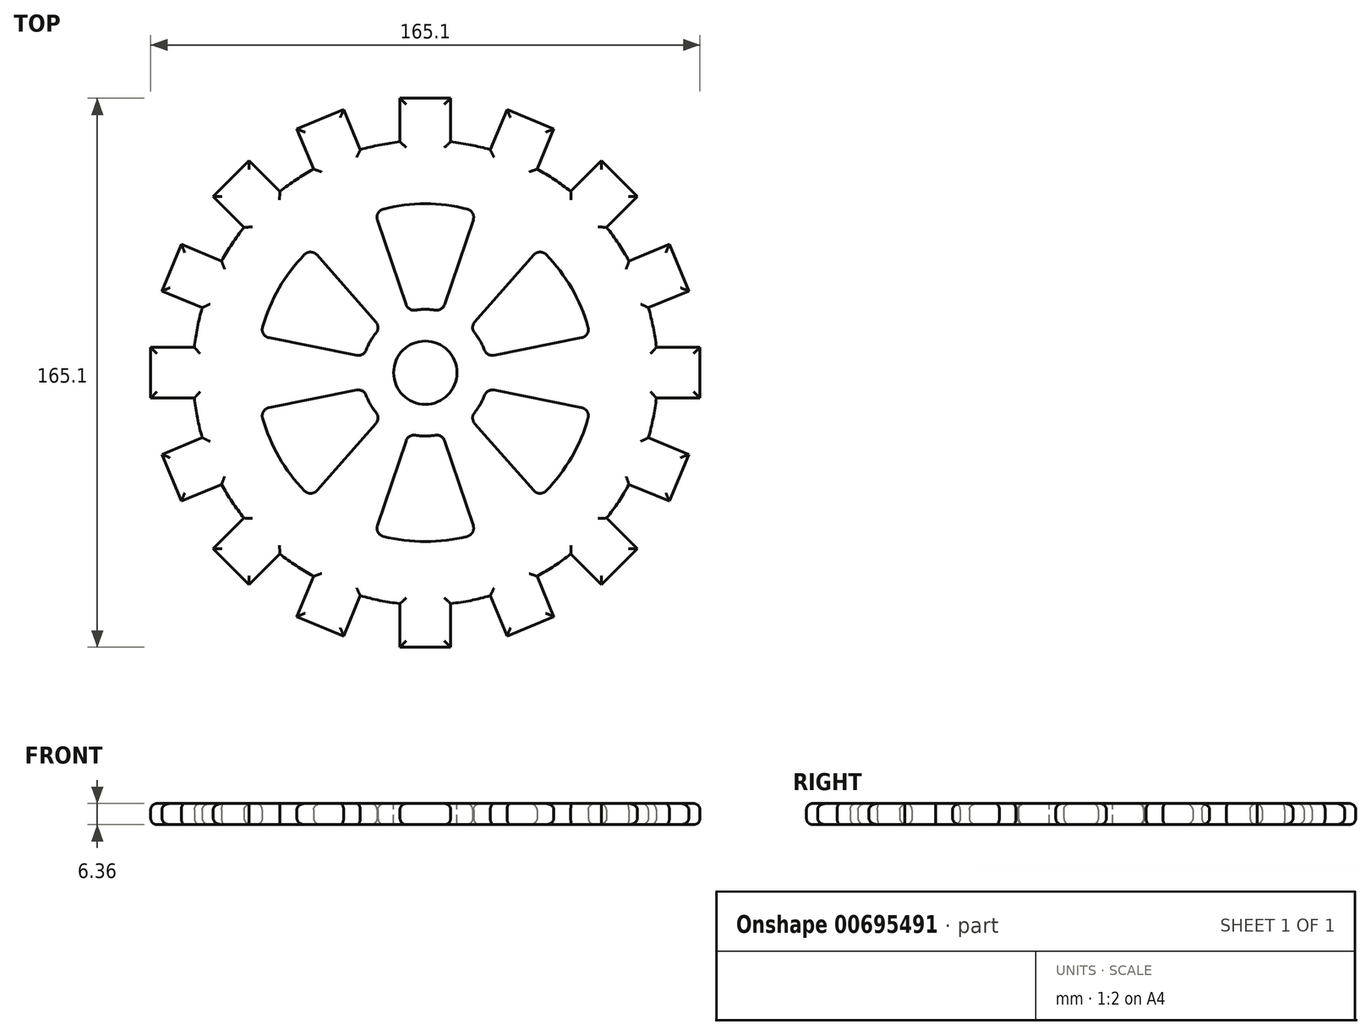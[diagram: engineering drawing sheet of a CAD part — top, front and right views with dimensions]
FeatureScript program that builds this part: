
annotation { "Feature Type Name" : "Feature", "Feature Type Description" : "" }
export const myFeature = defineFeature(function(context is Context, id is Id, definition is map)
    precondition{}
    {
        {
            var Q0;
            Q0=qCreatedBy(makeId("Top.planeOp"),FACE);
            var sketch = newSketch(context, id + "F0", { "sketchPlane" : qUnion([Q0])});
            skArc(sketch, "E0", {"start": v(-7.62, 69.43) * mm, "mid": v(-13.63, 68.5) * mm, "end": v(-19.53, 67.06) * mm});
            skLineSegment(sketch, "E1.top", {"start": v(-7.62, 82.55) * mm, "end": v(7.62, 82.55) * mm});
            skLineSegment(sketch, "E1.left", {"start": v(-7.62, 69.43) * mm, "end": v(-7.62, 82.55) * mm});
            skLineSegment(sketch, "E1.right", {"start": v(7.62, 69.43) * mm, "end": v(7.62, 82.55) * mm});
            skLineSegment(sketch, "E2.1.0", {"start": v(19.53, 67.06) * mm, "end": v(24.55, 79.18) * mm});
            skLineSegment(sketch, "E2.1.1", {"start": v(24.55, 79.18) * mm, "end": v(38.63, 73.35) * mm});
            skLineSegment(sketch, "E2.1.2", {"start": v(33.61, 61.23) * mm, "end": v(38.63, 73.35) * mm});
            skLineSegment(sketch, "E2.2.0", {"start": v(43.7, 54.48) * mm, "end": v(52.98, 63.76) * mm});
            skLineSegment(sketch, "E2.2.1", {"start": v(52.98, 63.76) * mm, "end": v(63.76, 52.98) * mm});
            skLineSegment(sketch, "E2.2.2", {"start": v(54.48, 43.7) * mm, "end": v(63.76, 52.98) * mm});
            skLineSegment(sketch, "E2.3.0", {"start": v(61.23, 33.61) * mm, "end": v(73.35, 38.63) * mm});
            skLineSegment(sketch, "E2.3.1", {"start": v(73.35, 38.63) * mm, "end": v(79.18, 24.55) * mm});
            skLineSegment(sketch, "E2.3.2", {"start": v(67.06, 19.53) * mm, "end": v(79.18, 24.55) * mm});
            skLineSegment(sketch, "E2.4.0", {"start": v(69.43, 7.62) * mm, "end": v(82.55, 7.62) * mm});
            skLineSegment(sketch, "E2.4.1", {"start": v(82.55, 7.62) * mm, "end": v(82.55, -7.62) * mm});
            skLineSegment(sketch, "E2.4.2", {"start": v(69.43, -7.62) * mm, "end": v(82.55, -7.62) * mm});
            skLineSegment(sketch, "E2.5.0", {"start": v(67.06, -19.53) * mm, "end": v(79.18, -24.55) * mm});
            skLineSegment(sketch, "E2.5.1", {"start": v(79.18, -24.55) * mm, "end": v(73.35, -38.63) * mm});
            skLineSegment(sketch, "E2.5.2", {"start": v(61.23, -33.61) * mm, "end": v(73.35, -38.63) * mm});
            skLineSegment(sketch, "E2.6.0", {"start": v(54.48, -43.7) * mm, "end": v(63.76, -52.98) * mm});
            skLineSegment(sketch, "E2.6.1", {"start": v(63.76, -52.98) * mm, "end": v(52.98, -63.76) * mm});
            skLineSegment(sketch, "E2.6.2", {"start": v(43.7, -54.48) * mm, "end": v(52.98, -63.76) * mm});
            skLineSegment(sketch, "E2.7.0", {"start": v(33.61, -61.23) * mm, "end": v(38.63, -73.35) * mm});
            skLineSegment(sketch, "E2.7.1", {"start": v(38.63, -73.35) * mm, "end": v(24.55, -79.18) * mm});
            skLineSegment(sketch, "E2.7.2", {"start": v(19.53, -67.06) * mm, "end": v(24.55, -79.18) * mm});
            skLineSegment(sketch, "E2.8.0", {"start": v(7.62, -69.43) * mm, "end": v(7.62, -82.55) * mm});
            skLineSegment(sketch, "E2.8.1", {"start": v(7.62, -82.55) * mm, "end": v(-7.62, -82.55) * mm});
            skLineSegment(sketch, "E2.8.2", {"start": v(-7.62, -69.43) * mm, "end": v(-7.62, -82.55) * mm});
            skLineSegment(sketch, "E2.9.0", {"start": v(-19.53, -67.06) * mm, "end": v(-24.55, -79.18) * mm});
            skLineSegment(sketch, "E2.9.1", {"start": v(-24.55, -79.18) * mm, "end": v(-38.63, -73.35) * mm});
            skLineSegment(sketch, "E2.9.2", {"start": v(-33.61, -61.23) * mm, "end": v(-38.63, -73.35) * mm});
            skLineSegment(sketch, "E2.10.0", {"start": v(-43.7, -54.48) * mm, "end": v(-52.98, -63.76) * mm});
            skLineSegment(sketch, "E2.10.1", {"start": v(-52.98, -63.76) * mm, "end": v(-63.76, -52.98) * mm});
            skLineSegment(sketch, "E2.10.2", {"start": v(-54.48, -43.7) * mm, "end": v(-63.76, -52.98) * mm});
            skLineSegment(sketch, "E2.11.0", {"start": v(-61.23, -33.61) * mm, "end": v(-73.35, -38.63) * mm});
            skLineSegment(sketch, "E2.11.1", {"start": v(-73.35, -38.63) * mm, "end": v(-79.18, -24.55) * mm});
            skLineSegment(sketch, "E2.11.2", {"start": v(-67.06, -19.53) * mm, "end": v(-79.18, -24.55) * mm});
            skLineSegment(sketch, "E2.12.0", {"start": v(-69.43, -7.62) * mm, "end": v(-82.55, -7.62) * mm});
            skLineSegment(sketch, "E2.12.1", {"start": v(-82.55, -7.62) * mm, "end": v(-82.55, 7.62) * mm});
            skLineSegment(sketch, "E2.12.2", {"start": v(-69.43, 7.62) * mm, "end": v(-82.55, 7.62) * mm});
            skLineSegment(sketch, "E2.13.0", {"start": v(-67.06, 19.53) * mm, "end": v(-79.18, 24.55) * mm});
            skLineSegment(sketch, "E2.13.1", {"start": v(-79.18, 24.55) * mm, "end": v(-73.35, 38.63) * mm});
            skLineSegment(sketch, "E2.13.2", {"start": v(-61.23, 33.61) * mm, "end": v(-73.35, 38.63) * mm});
            skLineSegment(sketch, "E2.14.0", {"start": v(-54.48, 43.7) * mm, "end": v(-63.76, 52.98) * mm});
            skLineSegment(sketch, "E2.14.1", {"start": v(-63.76, 52.98) * mm, "end": v(-52.98, 63.76) * mm});
            skLineSegment(sketch, "E2.14.2", {"start": v(-43.7, 54.48) * mm, "end": v(-52.98, 63.76) * mm});
            skLineSegment(sketch, "E2.15.0", {"start": v(-33.61, 61.23) * mm, "end": v(-38.63, 73.35) * mm});
            skLineSegment(sketch, "E2.15.1", {"start": v(-38.63, 73.35) * mm, "end": v(-24.55, 79.18) * mm});
            skLineSegment(sketch, "E2.15.2", {"start": v(-19.53, 67.06) * mm, "end": v(-24.55, 79.18) * mm});
            skLineSegment(sketch, "E2.anchor1", {"start": v(0, 0) * mm, "end": v(-7.62, 69.43) * mm, "construction": true});
            skLineSegment(sketch, "E2.anchor2", {"start": v(0, 0) * mm, "end": v(-33.61, 61.23) * mm, "construction": true});
            skArc(sketch, "E3.trimOffspring", {"start": v(-33.61, 61.23) * mm, "mid": v(-38.8, 58.08) * mm, "end": v(-43.7, 54.48) * mm});
            skArc(sketch, "E4.trimOffspring", {"start": v(19.53, 67.06) * mm, "mid": v(13.63, 68.5) * mm, "end": v(7.62, 69.43) * mm});
            skArc(sketch, "E5.trimOffspring", {"start": v(43.7, 54.48) * mm, "mid": v(38.8, 58.08) * mm, "end": v(33.61, 61.23) * mm});
            skArc(sketch, "E6.trimOffspring", {"start": v(61.23, 33.61) * mm, "mid": v(58.08, 38.8) * mm, "end": v(54.48, 43.7) * mm});
            skArc(sketch, "E7.trimOffspring", {"start": v(69.43, 7.62) * mm, "mid": v(68.5, 13.63) * mm, "end": v(67.06, 19.53) * mm});
            skArc(sketch, "E8.trimOffspring", {"start": v(67.06, -19.53) * mm, "mid": v(68.5, -13.63) * mm, "end": v(69.43, -7.62) * mm});
            skArc(sketch, "E9.trimOffspring", {"start": v(54.48, -43.7) * mm, "mid": v(58.08, -38.8) * mm, "end": v(61.23, -33.61) * mm});
            skArc(sketch, "E10.trimOffspring", {"start": v(33.61, -61.23) * mm, "mid": v(38.8, -58.08) * mm, "end": v(43.7, -54.48) * mm});
            skArc(sketch, "E11.trimOffspring", {"start": v(7.62, -69.43) * mm, "mid": v(13.63, -68.5) * mm, "end": v(19.53, -67.06) * mm});
            skArc(sketch, "E12.trimOffspring", {"start": v(-19.53, -67.06) * mm, "mid": v(-13.63, -68.5) * mm, "end": v(-7.62, -69.43) * mm});
            skArc(sketch, "E13.trimOffspring", {"start": v(-43.7, -54.48) * mm, "mid": v(-38.8, -58.08) * mm, "end": v(-33.61, -61.23) * mm});
            skArc(sketch, "E14.trimOffspring", {"start": v(-61.23, -33.61) * mm, "mid": v(-58.08, -38.8) * mm, "end": v(-54.48, -43.7) * mm});
            skArc(sketch, "E15.trimOffspring", {"start": v(-69.43, -7.62) * mm, "mid": v(-68.5, -13.63) * mm, "end": v(-67.06, -19.53) * mm});
            skArc(sketch, "E16.trimOffspring", {"start": v(-67.06, 19.53) * mm, "mid": v(-68.5, 13.63) * mm, "end": v(-69.43, 7.62) * mm});
            skArc(sketch, "E17.trimOffspring", {"start": v(-54.48, 43.7) * mm, "mid": v(-58.08, 38.8) * mm, "end": v(-61.23, 33.61) * mm});
            skArc(sketch, "E18", {"start": v(-3, -18.81) * mm, "mid": v(0, -19.05) * mm, "end": v(3, -18.81) * mm});
            skLineSegment(sketch, "E19", {"start": v(-14.39, -45.94) * mm, "end": v(-5.8, -20.5) * mm});
            skLineSegment(sketch, "E20.MirrorCS", {"start": v(14.39, -45.94) * mm, "end": v(5.8, -20.5) * mm});
            skArc(sketch, "E21.trimOffspring", {"start": v(-12.61, -49.2) * mm, "mid": v(0, -50.8) * mm, "end": v(12.61, -49.2) * mm});
            skLineSegment(sketch, "E22.1.0", {"start": v(-32.59, -35.43) * mm, "end": v(-14.86, -15.28) * mm});
            skArc(sketch, "E22.1.1", {"start": v(-17.8, -6.8) * mm, "mid": v(-16.5, -9.53) * mm, "end": v(-14.8, -12) * mm});
            skLineSegment(sketch, "E22.1.2", {"start": v(-46.98, -10.5) * mm, "end": v(-20.66, -5.23) * mm});
            skArc(sketch, "E22.1.3", {"start": v(-48.92, -13.68) * mm, "mid": v(-44, -25.4) * mm, "end": v(-36.31, -35.53) * mm});
            skLineSegment(sketch, "E22.2.0", {"start": v(-46.98, 10.5) * mm, "end": v(-20.66, 5.23) * mm});
            skArc(sketch, "E22.2.1", {"start": v(-14.8, 12) * mm, "mid": v(-16.5, 9.52) * mm, "end": v(-17.8, 6.8) * mm});
            skLineSegment(sketch, "E22.2.2", {"start": v(-32.59, 35.43) * mm, "end": v(-14.86, 15.28) * mm});
            skArc(sketch, "E22.2.3", {"start": v(-36.31, 35.53) * mm, "mid": v(-44, 25.4) * mm, "end": v(-48.92, 13.68) * mm});
            skLineSegment(sketch, "E22.3.0", {"start": v(-14.39, 45.94) * mm, "end": v(-5.8, 20.5) * mm});
            skArc(sketch, "E22.3.1", {"start": v(3, 18.81) * mm, "mid": v(0, 19.05) * mm, "end": v(-3, 18.81) * mm});
            skLineSegment(sketch, "E22.3.2", {"start": v(14.39, 45.94) * mm, "end": v(5.8, 20.5) * mm});
            skArc(sketch, "E22.3.3", {"start": v(12.61, 49.2) * mm, "mid": v(0, 50.8) * mm, "end": v(-12.61, 49.2) * mm});
            skLineSegment(sketch, "E22.4.0", {"start": v(32.59, 35.43) * mm, "end": v(14.86, 15.28) * mm});
            skArc(sketch, "E22.4.1", {"start": v(17.8, 6.8) * mm, "mid": v(16.5, 9.53) * mm, "end": v(14.8, 12) * mm});
            skLineSegment(sketch, "E22.4.2", {"start": v(46.98, 10.5) * mm, "end": v(20.66, 5.23) * mm});
            skArc(sketch, "E22.4.3", {"start": v(48.92, 13.68) * mm, "mid": v(44, 25.4) * mm, "end": v(36.31, 35.53) * mm});
            skLineSegment(sketch, "E22.5.0", {"start": v(46.98, -10.5) * mm, "end": v(20.66, -5.23) * mm});
            skArc(sketch, "E22.5.1", {"start": v(14.8, -12) * mm, "mid": v(16.5, -9.52) * mm, "end": v(17.8, -6.8) * mm});
            skLineSegment(sketch, "E22.5.2", {"start": v(32.59, -35.43) * mm, "end": v(14.86, -15.28) * mm});
            skArc(sketch, "E22.5.3", {"start": v(36.31, -35.53) * mm, "mid": v(44, -25.4) * mm, "end": v(48.92, -13.68) * mm});
            skLineSegment(sketch, "E22.anchor1", {"start": v(0, 0) * mm, "end": v(-15.24, -48.46) * mm, "construction": true});
            skLineSegment(sketch, "E22.anchor2", {"start": v(0, 0) * mm, "end": v(34.35, -37.43) * mm, "construction": true});
            skPoint(sketch, "E23.visualSharp", {"position": v(-34.35, 37.43) * mm});
            skArc(sketch, "E23.filletArc", {"start": v(-32.59, 35.43) * mm, "mid": v(-34.43, 36.3) * mm, "end": v(-36.31, 35.53) * mm});
            skPoint(sketch, "E24.visualSharp", {"position": v(-49.59, 11.03) * mm});
            skArc(sketch, "E24.filletArc", {"start": v(-48.92, 13.68) * mm, "mid": v(-48.64, 11.67) * mm, "end": v(-46.98, 10.5) * mm});
            skPoint(sketch, "E25.visualSharp", {"position": v(-18.44, 4.78) * mm});
            skArc(sketch, "E25.filletArc", {"start": v(-20.66, 5.23) * mm, "mid": v(-18.94, 5.5) * mm, "end": v(-17.8, 6.8) * mm});
            skPoint(sketch, "E26.visualSharp", {"position": v(-13.36, 13.58) * mm});
            skArc(sketch, "E26.filletArc", {"start": v(-14.8, 12) * mm, "mid": v(-14.23, 13.65) * mm, "end": v(-14.86, 15.28) * mm});
            skPoint(sketch, "E27.visualSharp", {"position": v(-18.44, -4.78) * mm});
            skArc(sketch, "E27.filletArc", {"start": v(-17.8, -6.8) * mm, "mid": v(-18.94, -5.5) * mm, "end": v(-20.66, -5.23) * mm});
            skPoint(sketch, "E28.visualSharp", {"position": v(-49.59, -11.03) * mm});
            skArc(sketch, "E28.filletArc", {"start": v(-46.98, -10.5) * mm, "mid": v(-48.64, -11.67) * mm, "end": v(-48.92, -13.68) * mm});
            skPoint(sketch, "E29.visualSharp", {"position": v(-34.35, -37.43) * mm});
            skArc(sketch, "E29.filletArc", {"start": v(-36.31, -35.53) * mm, "mid": v(-34.43, -36.3) * mm, "end": v(-32.59, -35.43) * mm});
            skPoint(sketch, "E30.visualSharp", {"position": v(-13.36, -13.58) * mm});
            skArc(sketch, "E30.filletArc", {"start": v(-14.86, -15.28) * mm, "mid": v(-14.23, -13.65) * mm, "end": v(-14.8, -12) * mm});
            skPoint(sketch, "E31.visualSharp", {"position": v(-5.08, -18.36) * mm});
            skArc(sketch, "E31.filletArc", {"start": v(-3, -18.81) * mm, "mid": v(-4.71, -19.15) * mm, "end": v(-5.8, -20.5) * mm});
            skPoint(sketch, "E32.visualSharp", {"position": v(5.08, -18.36) * mm});
            skArc(sketch, "E32.filletArc", {"start": v(5.8, -20.5) * mm, "mid": v(4.71, -19.15) * mm, "end": v(3, -18.81) * mm});
            skPoint(sketch, "E33.visualSharp", {"position": v(15.24, -48.46) * mm});
            skArc(sketch, "E33.filletArc", {"start": v(12.61, -49.2) * mm, "mid": v(14.21, -47.96) * mm, "end": v(14.39, -45.94) * mm});
            skPoint(sketch, "E34.visualSharp", {"position": v(-15.24, -48.46) * mm});
            skArc(sketch, "E34.filletArc", {"start": v(-14.39, -45.94) * mm, "mid": v(-14.21, -47.96) * mm, "end": v(-12.61, -49.2) * mm});
            skPoint(sketch, "E35.visualSharp", {"position": v(34.35, -37.43) * mm});
            skArc(sketch, "E35.filletArc", {"start": v(32.59, -35.43) * mm, "mid": v(34.43, -36.3) * mm, "end": v(36.31, -35.53) * mm});
            skPoint(sketch, "E36.visualSharp", {"position": v(49.59, -11.03) * mm});
            skArc(sketch, "E36.filletArc", {"start": v(48.92, -13.68) * mm, "mid": v(48.64, -11.67) * mm, "end": v(46.98, -10.5) * mm});
            skPoint(sketch, "E37.visualSharp", {"position": v(18.44, -4.78) * mm});
            skArc(sketch, "E37.filletArc", {"start": v(20.66, -5.23) * mm, "mid": v(18.94, -5.5) * mm, "end": v(17.8, -6.8) * mm});
            skPoint(sketch, "E38.visualSharp", {"position": v(13.36, -13.58) * mm});
            skArc(sketch, "E38.filletArc", {"start": v(14.8, -12) * mm, "mid": v(14.23, -13.65) * mm, "end": v(14.86, -15.28) * mm});
            skPoint(sketch, "E39.visualSharp", {"position": v(49.59, 11.03) * mm});
            skArc(sketch, "E39.filletArc", {"start": v(46.98, 10.5) * mm, "mid": v(48.64, 11.67) * mm, "end": v(48.92, 13.68) * mm});
            skPoint(sketch, "E40.visualSharp", {"position": v(13.36, 13.58) * mm});
            skArc(sketch, "E40.filletArc", {"start": v(14.86, 15.28) * mm, "mid": v(14.23, 13.65) * mm, "end": v(14.8, 12) * mm});
            skPoint(sketch, "E41.visualSharp", {"position": v(18.44, 4.78) * mm});
            skArc(sketch, "E41.filletArc", {"start": v(17.8, 6.8) * mm, "mid": v(18.94, 5.5) * mm, "end": v(20.66, 5.23) * mm});
            skPoint(sketch, "E42.visualSharp", {"position": v(5.08, 18.36) * mm});
            skArc(sketch, "E42.filletArc", {"start": v(3, 18.81) * mm, "mid": v(4.71, 19.15) * mm, "end": v(5.8, 20.5) * mm});
            skPoint(sketch, "E43.visualSharp", {"position": v(15.24, 48.46) * mm});
            skArc(sketch, "E43.filletArc", {"start": v(14.39, 45.94) * mm, "mid": v(14.21, 47.96) * mm, "end": v(12.61, 49.2) * mm});
            skPoint(sketch, "E44.visualSharp", {"position": v(-15.24, 48.46) * mm});
            skArc(sketch, "E44.filletArc", {"start": v(-12.61, 49.2) * mm, "mid": v(-14.21, 47.96) * mm, "end": v(-14.39, 45.94) * mm});
            skPoint(sketch, "E45.visualSharp", {"position": v(-5.08, 18.36) * mm});
            skArc(sketch, "E45.filletArc", {"start": v(-5.8, 20.5) * mm, "mid": v(-4.71, 19.15) * mm, "end": v(-3, 18.81) * mm});
            skPoint(sketch, "E46.visualSharp", {"position": v(34.35, 37.43) * mm});
            skArc(sketch, "E46.filletArc", {"start": v(36.31, 35.53) * mm, "mid": v(34.43, 36.3) * mm, "end": v(32.59, 35.43) * mm});
            skSolve(sketch);
        }
        {
            var Q0;
            Q0=makeQuery(id+"F0.imprint","IMPRINT",FACE,{"disambiguationData":[TD([[makeQuery(id+"F0.imprint","IMPRINT",EDGE,{"derivedFrom":sQuery(id+"F0.wireOp",EDGE,"E0")}),1.0]])]});
            extrude(context, id + "F1", {"entities" : qUnion([Q0]), "endBound" : BoundingType.SYMMETRIC, "depth" : 6.35 * mm, "offsetDistance" : 25.4 * mm});
        }
        {
            var Q0;
            Q0=makeQuery(id+"F1.opExtrude","CAP_FACE",FACE,{"disambiguationData":[OSD([sQuery(id+"F0.wireOp",EDGE,"E0"),sQuery(id+"F0.wireOp",EDGE,"E1.top"),sQuery(id+"F0.wireOp",EDGE,"E1.left"),sQuery(id+"F0.wireOp",EDGE,"E1.right"),sQuery(id+"F0.wireOp",EDGE,"E2.1.0"),sQuery(id+"F0.wireOp",EDGE,"E2.1.1"),sQuery(id+"F0.wireOp",EDGE,"E2.1.2"),sQuery(id+"F0.wireOp",EDGE,"E2.2.0"),sQuery(id+"F0.wireOp",EDGE,"E2.2.1"),sQuery(id+"F0.wireOp",EDGE,"E2.2.2"),sQuery(id+"F0.wireOp",EDGE,"E2.3.0"),sQuery(id+"F0.wireOp",EDGE,"E2.3.1"),sQuery(id+"F0.wireOp",EDGE,"E2.3.2"),sQuery(id+"F0.wireOp",EDGE,"E2.4.0"),sQuery(id+"F0.wireOp",EDGE,"E2.4.1"),sQuery(id+"F0.wireOp",EDGE,"E2.4.2"),sQuery(id+"F0.wireOp",EDGE,"E2.5.0"),sQuery(id+"F0.wireOp",EDGE,"E2.5.1"),sQuery(id+"F0.wireOp",EDGE,"E2.5.2"),sQuery(id+"F0.wireOp",EDGE,"E2.6.0"),sQuery(id+"F0.wireOp",EDGE,"E2.6.1"),sQuery(id+"F0.wireOp",EDGE,"E2.6.2"),sQuery(id+"F0.wireOp",EDGE,"E2.7.0"),sQuery(id+"F0.wireOp",EDGE,"E2.7.1"),sQuery(id+"F0.wireOp",EDGE,"E2.7.2"),sQuery(id+"F0.wireOp",EDGE,"E2.8.0"),sQuery(id+"F0.wireOp",EDGE,"E2.8.1"),sQuery(id+"F0.wireOp",EDGE,"E2.8.2"),sQuery(id+"F0.wireOp",EDGE,"E2.9.0"),sQuery(id+"F0.wireOp",EDGE,"E2.9.1"),sQuery(id+"F0.wireOp",EDGE,"E2.9.2"),sQuery(id+"F0.wireOp",EDGE,"E2.10.0"),sQuery(id+"F0.wireOp",EDGE,"E2.10.1"),sQuery(id+"F0.wireOp",EDGE,"E2.10.2"),sQuery(id+"F0.wireOp",EDGE,"E2.11.0"),sQuery(id+"F0.wireOp",EDGE,"E2.11.1"),sQuery(id+"F0.wireOp",EDGE,"E2.11.2"),sQuery(id+"F0.wireOp",EDGE,"E2.12.0"),sQuery(id+"F0.wireOp",EDGE,"E2.12.1"),sQuery(id+"F0.wireOp",EDGE,"E2.12.2"),sQuery(id+"F0.wireOp",EDGE,"E2.13.0"),sQuery(id+"F0.wireOp",EDGE,"E2.13.1"),sQuery(id+"F0.wireOp",EDGE,"E2.13.2"),sQuery(id+"F0.wireOp",EDGE,"E2.14.0"),sQuery(id+"F0.wireOp",EDGE,"E2.14.1"),sQuery(id+"F0.wireOp",EDGE,"E2.14.2"),sQuery(id+"F0.wireOp",EDGE,"E2.15.0"),sQuery(id+"F0.wireOp",EDGE,"E2.15.1"),sQuery(id+"F0.wireOp",EDGE,"E2.15.2"),sQuery(id+"F0.wireOp",EDGE,"E3.trimOffspring"),sQuery(id+"F0.wireOp",EDGE,"E4.trimOffspring"),sQuery(id+"F0.wireOp",EDGE,"E5.trimOffspring"),sQuery(id+"F0.wireOp",EDGE,"E6.trimOffspring"),sQuery(id+"F0.wireOp",EDGE,"E7.trimOffspring"),sQuery(id+"F0.wireOp",EDGE,"E8.trimOffspring"),sQuery(id+"F0.wireOp",EDGE,"E9.trimOffspring"),sQuery(id+"F0.wireOp",EDGE,"E10.trimOffspring"),sQuery(id+"F0.wireOp",EDGE,"E11.trimOffspring"),sQuery(id+"F0.wireOp",EDGE,"E12.trimOffspring"),sQuery(id+"F0.wireOp",EDGE,"E13.trimOffspring"),sQuery(id+"F0.wireOp",EDGE,"E14.trimOffspring"),sQuery(id+"F0.wireOp",EDGE,"E15.trimOffspring"),sQuery(id+"F0.wireOp",EDGE,"E16.trimOffspring"),sQuery(id+"F0.wireOp",EDGE,"E17.trimOffspring"),sQuery(id+"F0.wireOp",EDGE,"E18"),sQuery(id+"F0.wireOp",EDGE,"E19"),sQuery(id+"F0.wireOp",EDGE,"E20.MirrorCS"),sQuery(id+"F0.wireOp",EDGE,"E21.trimOffspring"),sQuery(id+"F0.wireOp",EDGE,"E22.1.0"),sQuery(id+"F0.wireOp",EDGE,"E22.1.1"),sQuery(id+"F0.wireOp",EDGE,"E22.1.2"),sQuery(id+"F0.wireOp",EDGE,"E22.1.3"),sQuery(id+"F0.wireOp",EDGE,"E22.2.0"),sQuery(id+"F0.wireOp",EDGE,"E22.2.1"),sQuery(id+"F0.wireOp",EDGE,"E22.2.2"),sQuery(id+"F0.wireOp",EDGE,"E22.2.3"),sQuery(id+"F0.wireOp",EDGE,"E22.3.0"),sQuery(id+"F0.wireOp",EDGE,"E22.3.1"),sQuery(id+"F0.wireOp",EDGE,"E22.3.2"),sQuery(id+"F0.wireOp",EDGE,"E22.3.3"),sQuery(id+"F0.wireOp",EDGE,"E22.4.0"),sQuery(id+"F0.wireOp",EDGE,"E22.4.1"),sQuery(id+"F0.wireOp",EDGE,"E22.4.2"),sQuery(id+"F0.wireOp",EDGE,"E22.4.3"),sQuery(id+"F0.wireOp",EDGE,"E22.5.0"),sQuery(id+"F0.wireOp",EDGE,"E22.5.1"),sQuery(id+"F0.wireOp",EDGE,"E22.5.2"),sQuery(id+"F0.wireOp",EDGE,"E22.5.3"),sQuery(id+"F0.wireOp",EDGE,"E23.filletArc"),sQuery(id+"F0.wireOp",EDGE,"E24.filletArc"),sQuery(id+"F0.wireOp",EDGE,"E25.filletArc"),sQuery(id+"F0.wireOp",EDGE,"E26.filletArc"),sQuery(id+"F0.wireOp",EDGE,"E27.filletArc"),sQuery(id+"F0.wireOp",EDGE,"E28.filletArc"),sQuery(id+"F0.wireOp",EDGE,"E29.filletArc"),sQuery(id+"F0.wireOp",EDGE,"E30.filletArc"),sQuery(id+"F0.wireOp",EDGE,"E31.filletArc"),sQuery(id+"F0.wireOp",EDGE,"E32.filletArc"),sQuery(id+"F0.wireOp",EDGE,"E33.filletArc"),sQuery(id+"F0.wireOp",EDGE,"E34.filletArc"),sQuery(id+"F0.wireOp",EDGE,"E35.filletArc"),sQuery(id+"F0.wireOp",EDGE,"E36.filletArc"),sQuery(id+"F0.wireOp",EDGE,"E37.filletArc"),sQuery(id+"F0.wireOp",EDGE,"E38.filletArc"),sQuery(id+"F0.wireOp",EDGE,"E39.filletArc"),sQuery(id+"F0.wireOp",EDGE,"E40.filletArc"),sQuery(id+"F0.wireOp",EDGE,"E41.filletArc"),sQuery(id+"F0.wireOp",EDGE,"E42.filletArc"),sQuery(id+"F0.wireOp",EDGE,"E43.filletArc"),sQuery(id+"F0.wireOp",EDGE,"E44.filletArc"),sQuery(id+"F0.wireOp",EDGE,"E45.filletArc"),sQuery(id+"F0.wireOp",EDGE,"E46.filletArc")])],"isStart":false});
            var Q1;
            Q1=makeQuery(id+"F1.opExtrude","CAP_FACE",FACE,{"disambiguationData":[OSD([sQuery(id+"F0.wireOp",EDGE,"E0"),sQuery(id+"F0.wireOp",EDGE,"E1.top"),sQuery(id+"F0.wireOp",EDGE,"E1.left"),sQuery(id+"F0.wireOp",EDGE,"E1.right"),sQuery(id+"F0.wireOp",EDGE,"E2.1.0"),sQuery(id+"F0.wireOp",EDGE,"E2.1.1"),sQuery(id+"F0.wireOp",EDGE,"E2.1.2"),sQuery(id+"F0.wireOp",EDGE,"E2.2.0"),sQuery(id+"F0.wireOp",EDGE,"E2.2.1"),sQuery(id+"F0.wireOp",EDGE,"E2.2.2"),sQuery(id+"F0.wireOp",EDGE,"E2.3.0"),sQuery(id+"F0.wireOp",EDGE,"E2.3.1"),sQuery(id+"F0.wireOp",EDGE,"E2.3.2"),sQuery(id+"F0.wireOp",EDGE,"E2.4.0"),sQuery(id+"F0.wireOp",EDGE,"E2.4.1"),sQuery(id+"F0.wireOp",EDGE,"E2.4.2"),sQuery(id+"F0.wireOp",EDGE,"E2.5.0"),sQuery(id+"F0.wireOp",EDGE,"E2.5.1"),sQuery(id+"F0.wireOp",EDGE,"E2.5.2"),sQuery(id+"F0.wireOp",EDGE,"E2.6.0"),sQuery(id+"F0.wireOp",EDGE,"E2.6.1"),sQuery(id+"F0.wireOp",EDGE,"E2.6.2"),sQuery(id+"F0.wireOp",EDGE,"E2.7.0"),sQuery(id+"F0.wireOp",EDGE,"E2.7.1"),sQuery(id+"F0.wireOp",EDGE,"E2.7.2"),sQuery(id+"F0.wireOp",EDGE,"E2.8.0"),sQuery(id+"F0.wireOp",EDGE,"E2.8.1"),sQuery(id+"F0.wireOp",EDGE,"E2.8.2"),sQuery(id+"F0.wireOp",EDGE,"E2.9.0"),sQuery(id+"F0.wireOp",EDGE,"E2.9.1"),sQuery(id+"F0.wireOp",EDGE,"E2.9.2"),sQuery(id+"F0.wireOp",EDGE,"E2.10.0"),sQuery(id+"F0.wireOp",EDGE,"E2.10.1"),sQuery(id+"F0.wireOp",EDGE,"E2.10.2"),sQuery(id+"F0.wireOp",EDGE,"E2.11.0"),sQuery(id+"F0.wireOp",EDGE,"E2.11.1"),sQuery(id+"F0.wireOp",EDGE,"E2.11.2"),sQuery(id+"F0.wireOp",EDGE,"E2.12.0"),sQuery(id+"F0.wireOp",EDGE,"E2.12.1"),sQuery(id+"F0.wireOp",EDGE,"E2.12.2"),sQuery(id+"F0.wireOp",EDGE,"E2.13.0"),sQuery(id+"F0.wireOp",EDGE,"E2.13.1"),sQuery(id+"F0.wireOp",EDGE,"E2.13.2"),sQuery(id+"F0.wireOp",EDGE,"E2.14.0"),sQuery(id+"F0.wireOp",EDGE,"E2.14.1"),sQuery(id+"F0.wireOp",EDGE,"E2.14.2"),sQuery(id+"F0.wireOp",EDGE,"E2.15.0"),sQuery(id+"F0.wireOp",EDGE,"E2.15.1"),sQuery(id+"F0.wireOp",EDGE,"E2.15.2"),sQuery(id+"F0.wireOp",EDGE,"E3.trimOffspring"),sQuery(id+"F0.wireOp",EDGE,"E4.trimOffspring"),sQuery(id+"F0.wireOp",EDGE,"E5.trimOffspring"),sQuery(id+"F0.wireOp",EDGE,"E6.trimOffspring"),sQuery(id+"F0.wireOp",EDGE,"E7.trimOffspring"),sQuery(id+"F0.wireOp",EDGE,"E8.trimOffspring"),sQuery(id+"F0.wireOp",EDGE,"E9.trimOffspring"),sQuery(id+"F0.wireOp",EDGE,"E10.trimOffspring"),sQuery(id+"F0.wireOp",EDGE,"E11.trimOffspring"),sQuery(id+"F0.wireOp",EDGE,"E12.trimOffspring"),sQuery(id+"F0.wireOp",EDGE,"E13.trimOffspring"),sQuery(id+"F0.wireOp",EDGE,"E14.trimOffspring"),sQuery(id+"F0.wireOp",EDGE,"E15.trimOffspring"),sQuery(id+"F0.wireOp",EDGE,"E16.trimOffspring"),sQuery(id+"F0.wireOp",EDGE,"E17.trimOffspring"),sQuery(id+"F0.wireOp",EDGE,"E18"),sQuery(id+"F0.wireOp",EDGE,"E19"),sQuery(id+"F0.wireOp",EDGE,"E20.MirrorCS"),sQuery(id+"F0.wireOp",EDGE,"E21.trimOffspring"),sQuery(id+"F0.wireOp",EDGE,"E22.1.0"),sQuery(id+"F0.wireOp",EDGE,"E22.1.1"),sQuery(id+"F0.wireOp",EDGE,"E22.1.2"),sQuery(id+"F0.wireOp",EDGE,"E22.1.3"),sQuery(id+"F0.wireOp",EDGE,"E22.2.0"),sQuery(id+"F0.wireOp",EDGE,"E22.2.1"),sQuery(id+"F0.wireOp",EDGE,"E22.2.2"),sQuery(id+"F0.wireOp",EDGE,"E22.2.3"),sQuery(id+"F0.wireOp",EDGE,"E22.3.0"),sQuery(id+"F0.wireOp",EDGE,"E22.3.1"),sQuery(id+"F0.wireOp",EDGE,"E22.3.2"),sQuery(id+"F0.wireOp",EDGE,"E22.3.3"),sQuery(id+"F0.wireOp",EDGE,"E22.4.0"),sQuery(id+"F0.wireOp",EDGE,"E22.4.1"),sQuery(id+"F0.wireOp",EDGE,"E22.4.2"),sQuery(id+"F0.wireOp",EDGE,"E22.4.3"),sQuery(id+"F0.wireOp",EDGE,"E22.5.0"),sQuery(id+"F0.wireOp",EDGE,"E22.5.1"),sQuery(id+"F0.wireOp",EDGE,"E22.5.2"),sQuery(id+"F0.wireOp",EDGE,"E22.5.3"),sQuery(id+"F0.wireOp",EDGE,"E23.filletArc"),sQuery(id+"F0.wireOp",EDGE,"E24.filletArc"),sQuery(id+"F0.wireOp",EDGE,"E25.filletArc"),sQuery(id+"F0.wireOp",EDGE,"E26.filletArc"),sQuery(id+"F0.wireOp",EDGE,"E27.filletArc"),sQuery(id+"F0.wireOp",EDGE,"E28.filletArc"),sQuery(id+"F0.wireOp",EDGE,"E29.filletArc"),sQuery(id+"F0.wireOp",EDGE,"E30.filletArc"),sQuery(id+"F0.wireOp",EDGE,"E31.filletArc"),sQuery(id+"F0.wireOp",EDGE,"E32.filletArc"),sQuery(id+"F0.wireOp",EDGE,"E33.filletArc"),sQuery(id+"F0.wireOp",EDGE,"E34.filletArc"),sQuery(id+"F0.wireOp",EDGE,"E35.filletArc"),sQuery(id+"F0.wireOp",EDGE,"E36.filletArc"),sQuery(id+"F0.wireOp",EDGE,"E37.filletArc"),sQuery(id+"F0.wireOp",EDGE,"E38.filletArc"),sQuery(id+"F0.wireOp",EDGE,"E39.filletArc"),sQuery(id+"F0.wireOp",EDGE,"E40.filletArc"),sQuery(id+"F0.wireOp",EDGE,"E41.filletArc"),sQuery(id+"F0.wireOp",EDGE,"E42.filletArc"),sQuery(id+"F0.wireOp",EDGE,"E43.filletArc"),sQuery(id+"F0.wireOp",EDGE,"E44.filletArc"),sQuery(id+"F0.wireOp",EDGE,"E45.filletArc"),sQuery(id+"F0.wireOp",EDGE,"E46.filletArc")])],"isStart":true});
            fillet(context, id + "F2", {"entities" : qUnion([Q0, Q1]), "radius" : 1.9 * mm, "tangentPropagation" : true, "allowEdgeOverflow" : false});
        }
        {
            var Q0;
            Q0=qCreatedBy(makeId("Top.planeOp"),FACE);
            var sketch = newSketch(context, id + "F3", { "sketchPlane" : qUnion([Q0])});
            skCircle(sketch, "E47", {"center": v(0, 0) * mm, "radius": 9.53 * mm});
            skSolve(sketch);
        }
        {
            var Q0;
            Q0 = qSketchRegion(id + "F3", true);
            var Q1;
            Q1=sQuery(id+"F3.wireOp",EDGE,"E47");
            extrude(context, id + "F4", {"entities" : qUnion([Q0]), "operationType" : NewBodyOperationType.REMOVE, "surfaceEntities" : qUnion([Q1]), "endBound" : BoundingType.SYMMETRIC, "oppositeDirection" : true, "depth" : 50.8 * mm, "offsetDistance" : 25.4 * mm});
        }
    });
